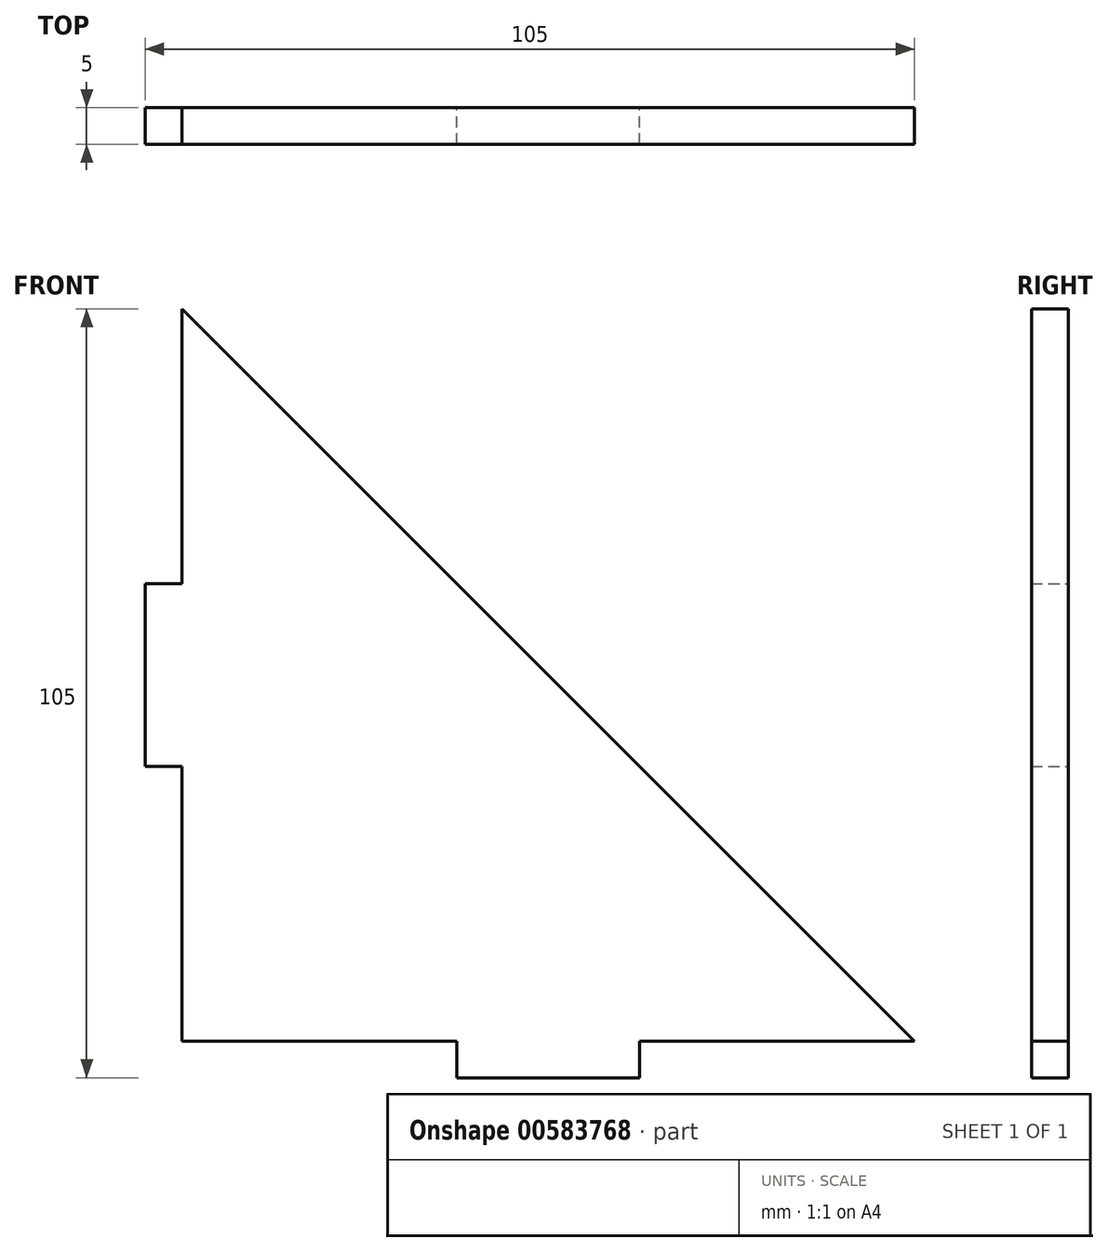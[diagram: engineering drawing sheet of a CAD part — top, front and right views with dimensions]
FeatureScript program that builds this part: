
annotation { "Feature Type Name" : "Feature", "Feature Type Description" : "" }
export const myFeature = defineFeature(function(context is Context, id is Id, definition is map)
    precondition{}
    {
        {
            var Q0;
            Q0=qCreatedBy(makeId("Front.planeOp"),FACE);
            var sketch = newSketch(context, id + "F0", { "sketchPlane" : qUnion([Q0])});
            skLineSegment(sketch, "E0", {"start": v(-99.79, -59.77) * mm, "end": v(-62.29, -59.77) * mm});
            skLineSegment(sketch, "E1", {"start": v(-99.79, -59.77) * mm, "end": v(-99.79, -22.27) * mm});
            skLineSegment(sketch, "E2", {"start": v(-99.79, -22.27) * mm, "end": v(-104.79, -22.27) * mm});
            skLineSegment(sketch, "E3", {"start": v(-104.79, -22.27) * mm, "end": v(-104.79, 2.73) * mm});
            skLineSegment(sketch, "E4", {"start": v(-104.79, 2.73) * mm, "end": v(-99.79, 2.73) * mm});
            skLineSegment(sketch, "E5", {"start": v(-99.79, 2.73) * mm, "end": v(-99.79, 40.23) * mm});
            skLineSegment(sketch, "E6", {"start": v(-99.79, 40.23) * mm, "end": v(0.21, -59.77) * mm});
            skLineSegment(sketch, "E7", {"start": v(0.21, -59.77) * mm, "end": v(-37.29, -59.77) * mm});
            skLineSegment(sketch, "E8", {"start": v(-37.29, -59.77) * mm, "end": v(-37.29, -64.77) * mm});
            skLineSegment(sketch, "E9", {"start": v(-62.29, -59.77) * mm, "end": v(-62.29, -64.77) * mm});
            skLineSegment(sketch, "E10", {"start": v(-62.29, -64.77) * mm, "end": v(-37.29, -64.77) * mm});
            skSolve(sketch);
        }
        {
            var Q0;
            Q0=makeQuery(id+"F0.imprint","IMPRINT",FACE,{"disambiguationData":[TD([[makeQuery(id+"F0.imprint","IMPRINT",EDGE,{"derivedFrom":sQuery(id+"F0.wireOp",EDGE,"E0")}),1.0]])]});
            extrude(context, id + "F1", {"entities" : qUnion([Q0]), "depth" : 5 * mm, "offsetDistance" : 25 * mm});
        }
    });
